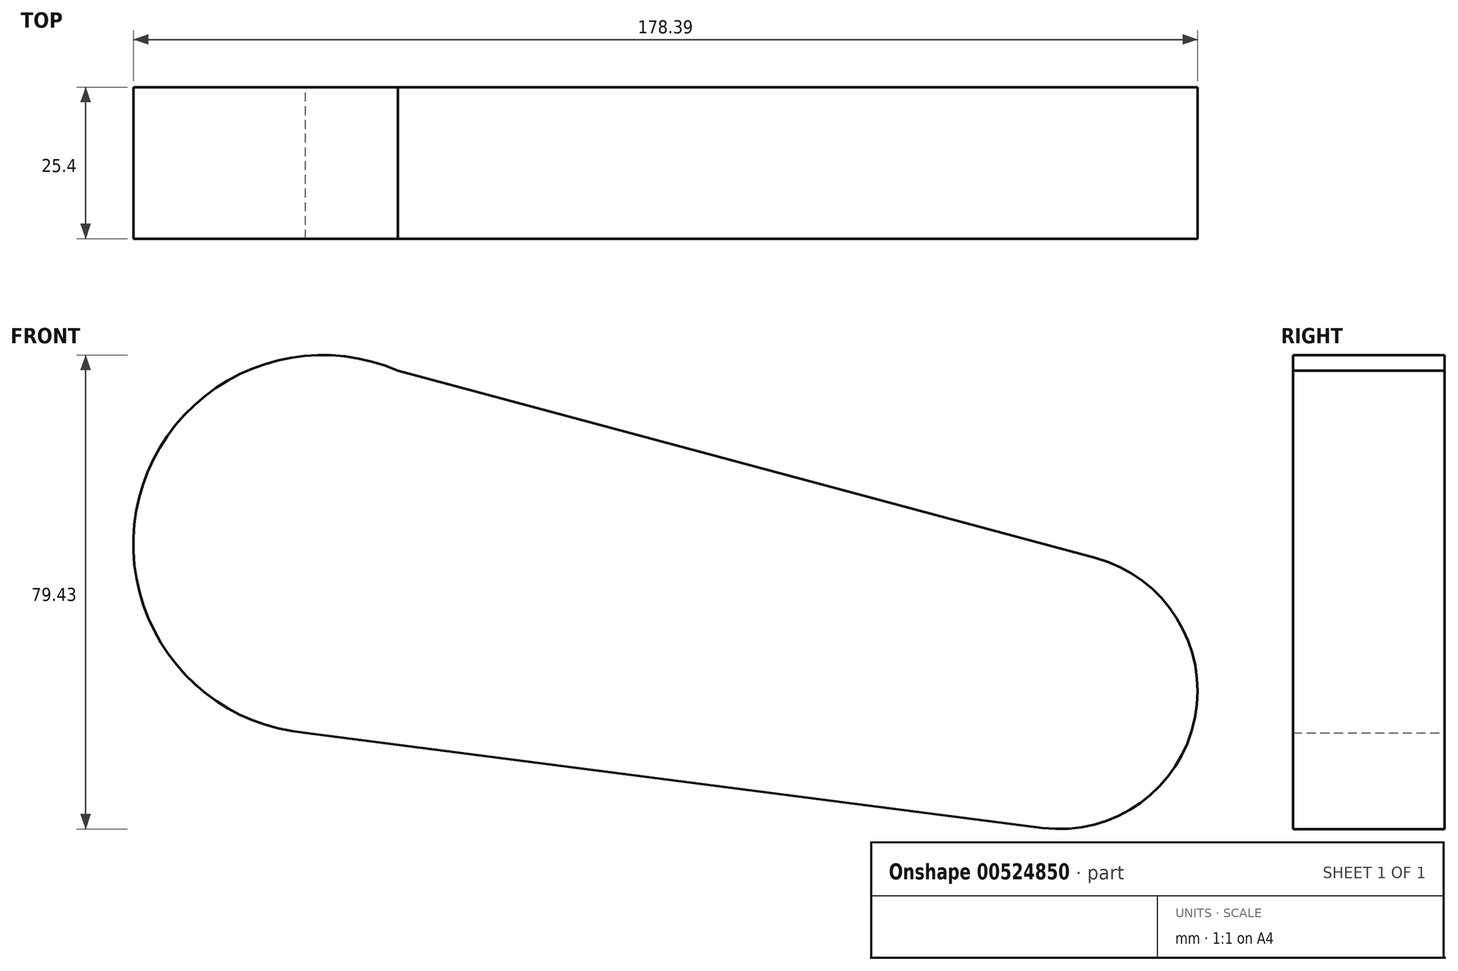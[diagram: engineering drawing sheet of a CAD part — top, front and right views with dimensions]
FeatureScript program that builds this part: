
annotation { "Feature Type Name" : "Feature", "Feature Type Description" : "" }
export const myFeature = defineFeature(function(context is Context, id is Id, definition is map)
    precondition{}
    {
        {
            var Q0;
            Q0=qCreatedBy(makeId("Front.planeOp"),FACE);
            var sketch = newSketch(context, id + "F0", { "sketchPlane" : qUnion([Q0])});
            skCircle(sketch, "E0", {"center": v(-63.37, 39.5) * mm, "radius": 31.73 * mm});
            skCircle(sketch, "E1", {"center": v(60.19, 14.9) * mm, "radius": 23.1 * mm});
            skLineSegment(sketch, "E2", {"start": v(-59.69, 71.02) * mm, "end": v(66.18, 37.22) * mm});
            skLineSegment(sketch, "E3", {"start": v(-66.24, 7.9) * mm, "end": v(57.24, -8.01) * mm});
            skSolve(sketch);
        }
        {
            var Q0;
            Q0 = qSketchRegion(id + "F0", true);
            extrude(context, id + "F1", {"entities" : qUnion([Q0]), "depth" : 25.4 * mm, "offsetDistance" : 25.4 * mm});
        }
        {
            var Q0;
            Q0 = qSketchRegion(id + "F0", true);
            extrude(context, id + "F2", {"entities" : qUnion([Q0]), "operationType" : NewBodyOperationType.ADD, "depth" : 25.4 * mm, "offsetDistance" : 25.4 * mm});
        }
    });
